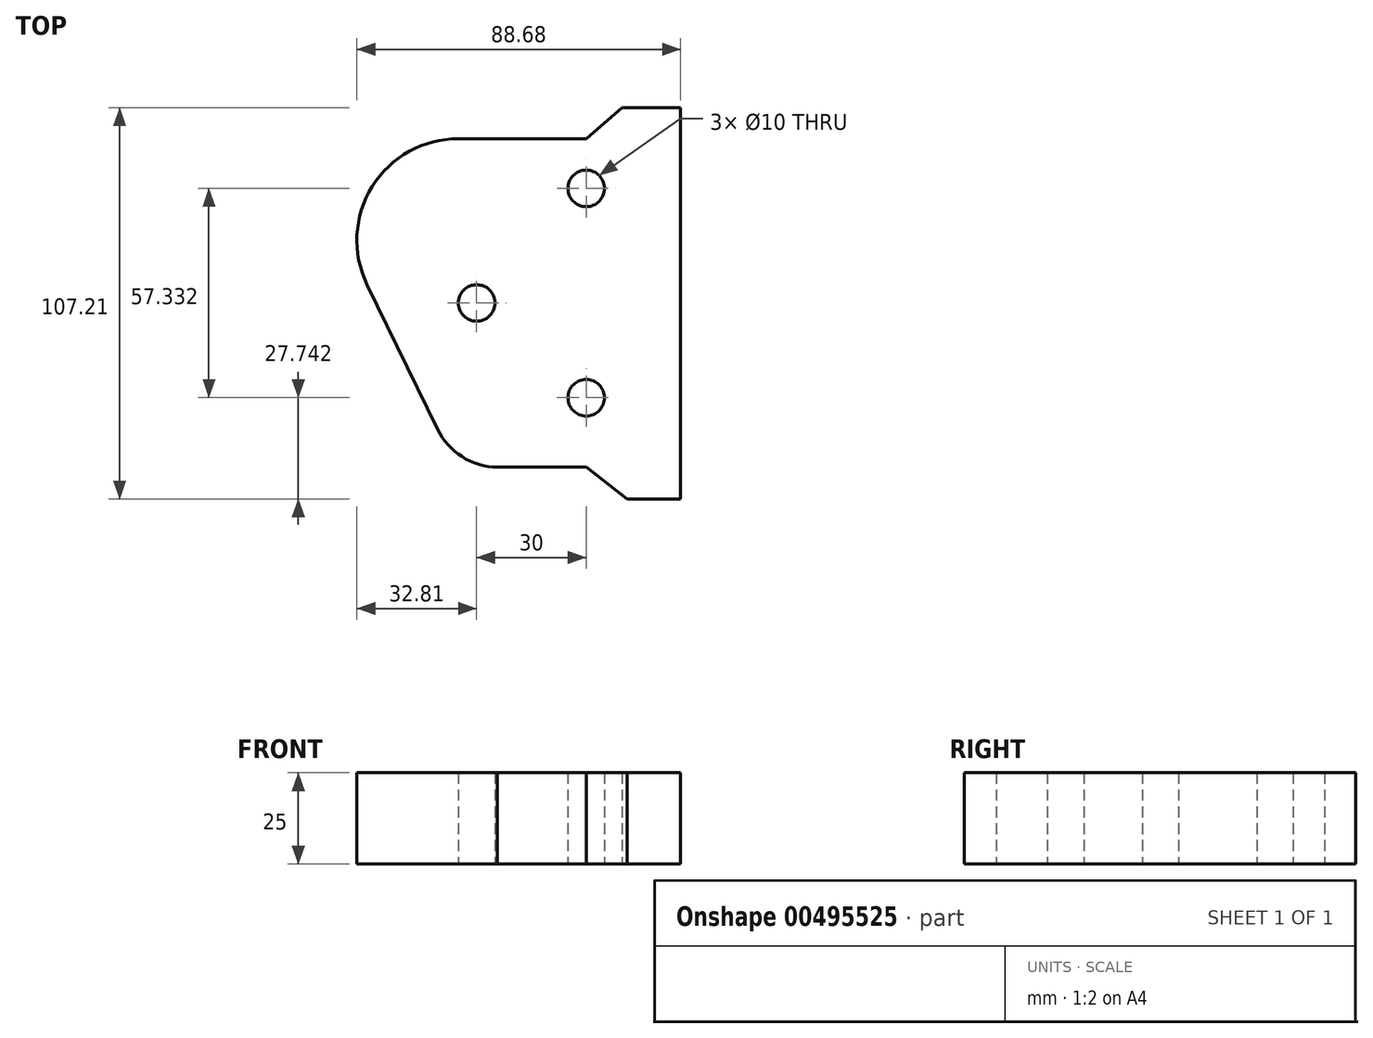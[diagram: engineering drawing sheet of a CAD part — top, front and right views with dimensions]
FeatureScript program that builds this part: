
annotation { "Feature Type Name" : "Feature", "Feature Type Description" : "" }
export const myFeature = defineFeature(function(context is Context, id is Id, definition is map)
    precondition{}
    {
        {
            var Q0;
            Q0=qCreatedBy(makeId("Top.planeOp"),FACE);
            var sketch = newSketch(context, id + "F0", { "sketchPlane" : qUnion([Q0])});
            skLineSegment(sketch, "E0.bottom", {"start": v(30, 45) * mm, "end": v(-30, 45) * mm, "construction": true});
            skLineSegment(sketch, "E0.top", {"start": v(30, -45) * mm, "end": v(-30, -45) * mm, "construction": true});
            skLineSegment(sketch, "E0.left", {"start": v(30, 45) * mm, "end": v(30, -45) * mm, "construction": true});
            skLineSegment(sketch, "E0.right", {"start": v(-30, 45) * mm, "end": v(-30, -45) * mm, "construction": true});
            skPoint(sketch, "E0.middle", {"position": v(0, 0) * mm});
            skLineSegment(sketch, "E1", {"start": v(30, 45) * mm, "end": v(-5, 45) * mm, "construction": true});
            skLineSegment(sketch, "E2", {"start": v(30, 45) * mm, "end": v(-5, 45) * mm});
            skLineSegment(sketch, "E3.bottom", {"start": v(-30, 45) * mm, "end": v(-5, 45) * mm, "construction": true});
            skLineSegment(sketch, "E3.top", {"start": v(-30, 5) * mm, "end": v(-5, 5) * mm, "construction": true});
            skLineSegment(sketch, "E3.left", {"start": v(-30, 45) * mm, "end": v(-30, 5) * mm, "construction": true});
            skLineSegment(sketch, "E3.right", {"start": v(-5, 45) * mm, "end": v(-5, 5) * mm, "construction": true});
            skArc(sketch, "E4", {"start": v(-5, 45) * mm, "mid": v(-28.58, 31.93) * mm, "end": v(-30, 5) * mm});
            skLineSegment(sketch, "E5", {"start": v(-30, 5) * mm, "end": v(-10.7, -34.57) * mm});
            skArc(sketch, "E6", {"start": v(-10.7, -34.57) * mm, "mid": v(-4, -42.09) * mm, "end": v(5.63, -45) * mm});
            skLineSegment(sketch, "E7", {"start": v(5.63, -45) * mm, "end": v(30, -45) * mm});
            skLineSegment(sketch, "E8", {"start": v(30, 45) * mm, "end": v(39.87, 53.51) * mm});
            skLineSegment(sketch, "E9", {"start": v(39.87, 53.51) * mm, "end": v(55.87, 53.51) * mm});
            skLineSegment(sketch, "E10", {"start": v(55.87, 53.51) * mm, "end": v(55.87, -53.7) * mm});
            skLineSegment(sketch, "E11", {"start": v(55.87, -53.7) * mm, "end": v(41.18, -53.7) * mm});
            skLineSegment(sketch, "E12", {"start": v(41.18, -53.7) * mm, "end": v(30, -45) * mm});
            skCircle(sketch, "E13", {"center": v(0, 0) * mm, "radius": 5 * mm});
            skCircle(sketch, "E14", {"center": v(30, 31.37) * mm, "radius": 5 * mm});
            skCircle(sketch, "E15", {"center": v(30, -25.96) * mm, "radius": 5 * mm});
            skSolve(sketch);
        }
        {
            var Q0;
            Q0=makeQuery(id+"F0.imprint","IMPRINT",FACE,{"disambiguationData":[TD([[makeQuery(id+"F0.imprint","IMPRINT",EDGE,{"derivedFrom":sQuery(id+"F0.wireOp",EDGE,"E2")}),1.0]])]});
            extrude(context, id + "F1", {"entities" : qUnion([Q0]), "depth" : 25 * mm});
        }
    });
